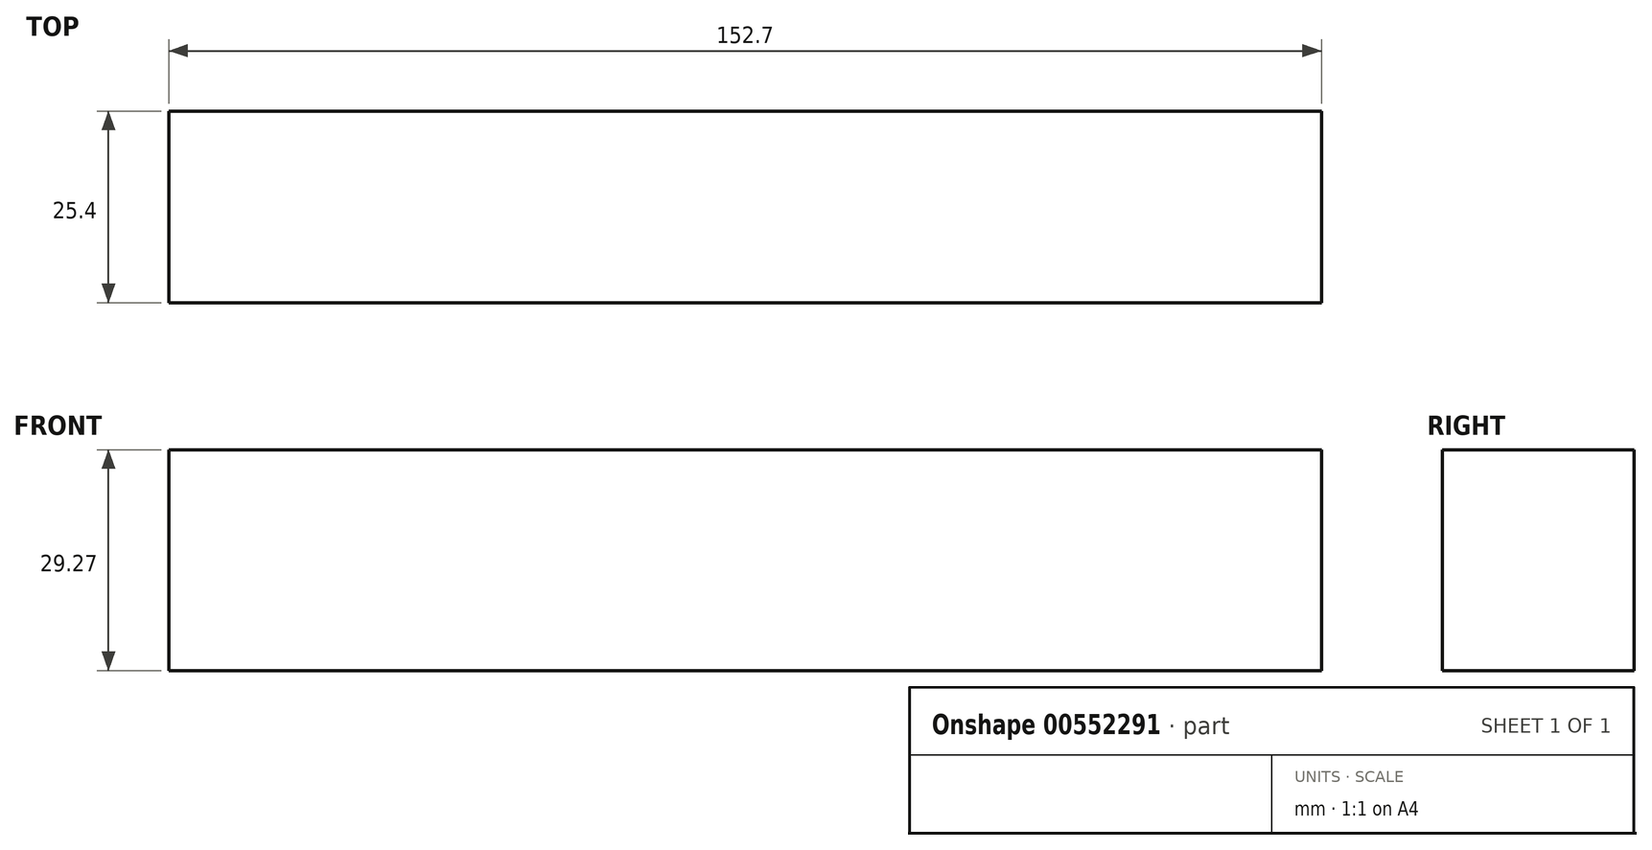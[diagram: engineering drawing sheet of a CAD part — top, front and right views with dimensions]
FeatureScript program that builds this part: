
annotation { "Feature Type Name" : "Feature", "Feature Type Description" : "" }
export const myFeature = defineFeature(function(context is Context, id is Id, definition is map)
    precondition{}
    {
        {
            var Q0;
            Q0=qCreatedBy(makeId("Front.planeOp"),FACE);
            var sketch = newSketch(context, id + "F0", { "sketchPlane" : qUnion([Q0])});
            skLineSegment(sketch, "E0.bottom", {"start": v(-76.86, 58.28) * mm, "end": v(75.84, 58.28) * mm});
            skLineSegment(sketch, "E0.top", {"start": v(-76.86, 29.01) * mm, "end": v(75.84, 29.01) * mm});
            skLineSegment(sketch, "E0.left", {"start": v(-76.86, 58.28) * mm, "end": v(-76.86, 29.01) * mm});
            skLineSegment(sketch, "E0.right", {"start": v(75.84, 58.28) * mm, "end": v(75.84, 29.01) * mm});
            skSolve(sketch);
        }
        {
            var Q0;
            Q0=makeQuery(id+"F0.imprint","IMPRINT",FACE,{"disambiguationData":[TD([[makeQuery(id+"F0.imprint","IMPRINT",EDGE,{"derivedFrom":sQuery(id+"F0.wireOp",EDGE,"E0.bottom")}),-1.0]])]});
            extrude(context, id + "F1", {"entities" : qUnion([Q0]), "depth" : 25.4 * mm, "offsetDistance" : 25.4 * mm});
        }
    });
